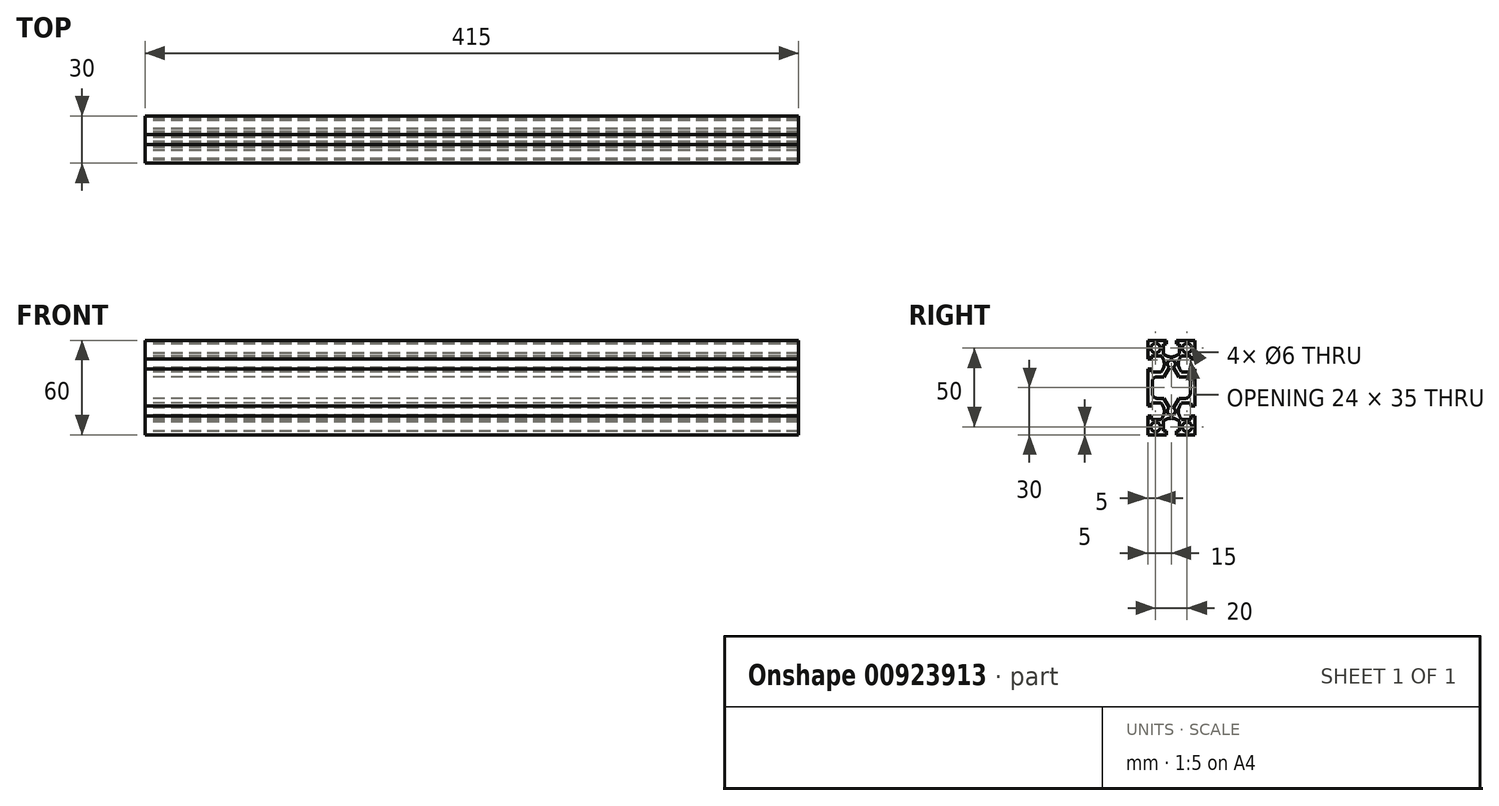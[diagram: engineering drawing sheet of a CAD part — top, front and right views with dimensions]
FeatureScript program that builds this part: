
annotation { "Feature Type Name" : "Feature", "Feature Type Description" : "" }
export const myFeature = defineFeature(function(context is Context, id is Id, definition is map)
    precondition{}
    {
        {
            var Q0;
            Q0=qCreatedBy(makeId("Right.planeOp"),FACE);
            var sketch = newSketch(context, id + "F0", { "sketchPlane" : qUnion([Q0])});
            skArc(sketch, "E0", {"start": v(-9, 6.85) * mm, "mid": v(-11.12, 5.97) * mm, "end": v(-12, 3.85) * mm});
            skLineSegment(sketch, "E1", {"start": v(-9, 6.85) * mm, "end": v(-4.7, 6.85) * mm});
            skLineSegment(sketch, "E2", {"start": v(-4.7, 6.85) * mm, "end": v(-1.25, 12.83) * mm});
            skArc(sketch, "E3", {"start": v(1.25, 12.83) * mm, "mid": v(0, 17.5) * mm, "end": v(-1.25, 12.83) * mm});
            skLineSegment(sketch, "E4", {"start": v(1.25, 12.83) * mm, "end": v(4.7, 6.85) * mm});
            skLineSegment(sketch, "E5", {"start": v(4.7, 6.85) * mm, "end": v(9, 6.85) * mm});
            skArc(sketch, "E6", {"start": v(12, 3.85) * mm, "mid": v(11.12, 5.97) * mm, "end": v(9, 6.85) * mm});
            skLineSegment(sketch, "E7", {"start": v(12, 3.85) * mm, "end": v(12, -3.85) * mm});
            skArc(sketch, "E8", {"start": v(9, -6.85) * mm, "mid": v(11.12, -5.97) * mm, "end": v(12, -3.85) * mm});
            skLineSegment(sketch, "E9", {"start": v(9, -6.85) * mm, "end": v(4.7, -6.85) * mm});
            skLineSegment(sketch, "E10", {"start": v(4.7, -6.85) * mm, "end": v(1.25, -12.83) * mm});
            skArc(sketch, "E11", {"start": v(-1.25, -12.83) * mm, "mid": v(0, -17.5) * mm, "end": v(1.25, -12.83) * mm});
            skLineSegment(sketch, "E12", {"start": v(-1.25, -12.83) * mm, "end": v(-4.7, -6.85) * mm});
            skLineSegment(sketch, "E13", {"start": v(-4.7, -6.85) * mm, "end": v(-9, -6.85) * mm});
            skArc(sketch, "E14", {"start": v(-12, -3.85) * mm, "mid": v(-11.12, -5.97) * mm, "end": v(-9, -6.85) * mm});
            skLineSegment(sketch, "E15", {"start": v(-12, -3.85) * mm, "end": v(-12, 3.85) * mm});
            skCircle(sketch, "E16", {"center": v(-10, 25) * mm, "radius": 3 * mm});
            skCircle(sketch, "E17", {"center": v(10, 25) * mm, "radius": 3 * mm});
            skCircle(sketch, "E18", {"center": v(-10, -25) * mm, "radius": 3 * mm});
            skCircle(sketch, "E19", {"center": v(10, -25) * mm, "radius": 3 * mm});
            skLineSegment(sketch, "E20", {"start": v(15, -11.85) * mm, "end": v(12.5, -11.85) * mm});
            skLineSegment(sketch, "E21", {"start": v(12.5, -11.85) * mm, "end": v(12.5, -9.85) * mm});
            skLineSegment(sketch, "E22", {"start": v(12.5, -9.85) * mm, "end": v(6.55, -9.85) * mm});
            skArc(sketch, "E23", {"start": v(6.55, -9.85) * mm, "mid": v(4.5, -15) * mm, "end": v(6.55, -20.15) * mm});
            skLineSegment(sketch, "E24", {"start": v(6.55, -20.15) * mm, "end": v(12.5, -20.15) * mm});
            skLineSegment(sketch, "E25", {"start": v(12.5, -20.15) * mm, "end": v(12.5, -18.15) * mm});
            skLineSegment(sketch, "E26", {"start": v(12.5, -18.15) * mm, "end": v(15, -18.15) * mm});
            skLineSegment(sketch, "E27", {"start": v(15, -18.15) * mm, "end": v(15, -30) * mm});
            skLineSegment(sketch, "E28", {"start": v(15, -30) * mm, "end": v(3.15, -30) * mm});
            skLineSegment(sketch, "E29", {"start": v(3.15, -30) * mm, "end": v(3.15, -27.5) * mm});
            skLineSegment(sketch, "E30", {"start": v(3.15, -27.5) * mm, "end": v(5.15, -27.5) * mm});
            skLineSegment(sketch, "E31", {"start": v(5.15, -27.5) * mm, "end": v(5.15, -21.55) * mm});
            skArc(sketch, "E32", {"start": v(5.15, -21.55) * mm, "mid": v(0, -19.5) * mm, "end": v(-5.15, -21.55) * mm});
            skLineSegment(sketch, "E33", {"start": v(-5.15, -21.55) * mm, "end": v(-5.15, -27.5) * mm});
            skLineSegment(sketch, "E34", {"start": v(-5.15, -27.5) * mm, "end": v(-3.15, -27.5) * mm});
            skLineSegment(sketch, "E35", {"start": v(-3.15, -27.5) * mm, "end": v(-3.15, -30) * mm});
            skLineSegment(sketch, "E36", {"start": v(-3.15, -30) * mm, "end": v(-15, -30) * mm});
            skLineSegment(sketch, "E37", {"start": v(-15, -30) * mm, "end": v(-15, -18.15) * mm});
            skLineSegment(sketch, "E38", {"start": v(-15, -18.15) * mm, "end": v(-12.5, -18.15) * mm});
            skLineSegment(sketch, "E39", {"start": v(-12.5, -18.15) * mm, "end": v(-12.5, -20.15) * mm});
            skLineSegment(sketch, "E40", {"start": v(-12.5, -20.15) * mm, "end": v(-6.55, -20.15) * mm});
            skArc(sketch, "E41", {"start": v(-6.55, -20.15) * mm, "mid": v(-4.5, -15) * mm, "end": v(-6.55, -9.85) * mm});
            skLineSegment(sketch, "E42", {"start": v(-6.55, -9.85) * mm, "end": v(-12.5, -9.85) * mm});
            skLineSegment(sketch, "E43", {"start": v(-12.5, -9.85) * mm, "end": v(-12.5, -11.85) * mm});
            skLineSegment(sketch, "E44", {"start": v(-12.5, -11.85) * mm, "end": v(-15, -11.85) * mm});
            skLineSegment(sketch, "E45", {"start": v(-15, -11.85) * mm, "end": v(-15, 11.85) * mm});
            skLineSegment(sketch, "E46", {"start": v(-15, 11.85) * mm, "end": v(-12.5, 11.85) * mm});
            skLineSegment(sketch, "E47", {"start": v(-12.5, 11.85) * mm, "end": v(-12.5, 9.85) * mm});
            skLineSegment(sketch, "E48", {"start": v(-12.5, 9.85) * mm, "end": v(-6.55, 9.85) * mm});
            skArc(sketch, "E49", {"start": v(-6.55, 9.85) * mm, "mid": v(-4.5, 15) * mm, "end": v(-6.55, 20.15) * mm});
            skLineSegment(sketch, "E50", {"start": v(-6.55, 20.15) * mm, "end": v(-12.5, 20.15) * mm});
            skLineSegment(sketch, "E51", {"start": v(-12.5, 20.15) * mm, "end": v(-12.5, 18.15) * mm});
            skLineSegment(sketch, "E52", {"start": v(-12.5, 18.15) * mm, "end": v(-15, 18.15) * mm});
            skLineSegment(sketch, "E53", {"start": v(-15, 18.15) * mm, "end": v(-15, 30) * mm});
            skLineSegment(sketch, "E54", {"start": v(-15, 30) * mm, "end": v(-3.15, 30) * mm});
            skLineSegment(sketch, "E55", {"start": v(-3.15, 30) * mm, "end": v(-3.15, 27.5) * mm});
            skLineSegment(sketch, "E56", {"start": v(-3.15, 27.5) * mm, "end": v(-5.15, 27.5) * mm});
            skLineSegment(sketch, "E57", {"start": v(-5.15, 27.5) * mm, "end": v(-5.15, 21.55) * mm});
            skArc(sketch, "E58", {"start": v(-5.15, 21.55) * mm, "mid": v(0, 19.5) * mm, "end": v(5.15, 21.55) * mm});
            skLineSegment(sketch, "E59", {"start": v(5.15, 21.55) * mm, "end": v(5.15, 27.5) * mm});
            skLineSegment(sketch, "E60", {"start": v(5.15, 27.5) * mm, "end": v(3.15, 27.5) * mm});
            skLineSegment(sketch, "E61", {"start": v(3.15, 27.5) * mm, "end": v(3.15, 30) * mm});
            skLineSegment(sketch, "E62", {"start": v(3.15, 30) * mm, "end": v(15, 30) * mm});
            skLineSegment(sketch, "E63", {"start": v(15, 30) * mm, "end": v(15, 18.15) * mm});
            skLineSegment(sketch, "E64", {"start": v(15, 18.15) * mm, "end": v(12.5, 18.15) * mm});
            skLineSegment(sketch, "E65", {"start": v(12.5, 18.15) * mm, "end": v(12.5, 20.15) * mm});
            skLineSegment(sketch, "E66", {"start": v(12.5, 20.15) * mm, "end": v(6.55, 20.15) * mm});
            skArc(sketch, "E67", {"start": v(6.55, 20.15) * mm, "mid": v(4.5, 15) * mm, "end": v(6.55, 9.85) * mm});
            skLineSegment(sketch, "E68", {"start": v(6.55, 9.85) * mm, "end": v(12.5, 9.85) * mm});
            skLineSegment(sketch, "E69", {"start": v(12.5, 9.85) * mm, "end": v(12.5, 11.85) * mm});
            skLineSegment(sketch, "E70", {"start": v(12.5, 11.85) * mm, "end": v(15, 11.85) * mm});
            skLineSegment(sketch, "E71", {"start": v(15, 11.85) * mm, "end": v(15, -11.85) * mm});
            skSolve(sketch);
        }
        {
            var Q0;
            Q0=qSketchRegion(id+"F0",true);
            extrude(context, id + "F1", {"entities" : qUnion([Q0]), "depth" : 415 * mm, "offsetDistance" : 25 * mm});
        }
    });
